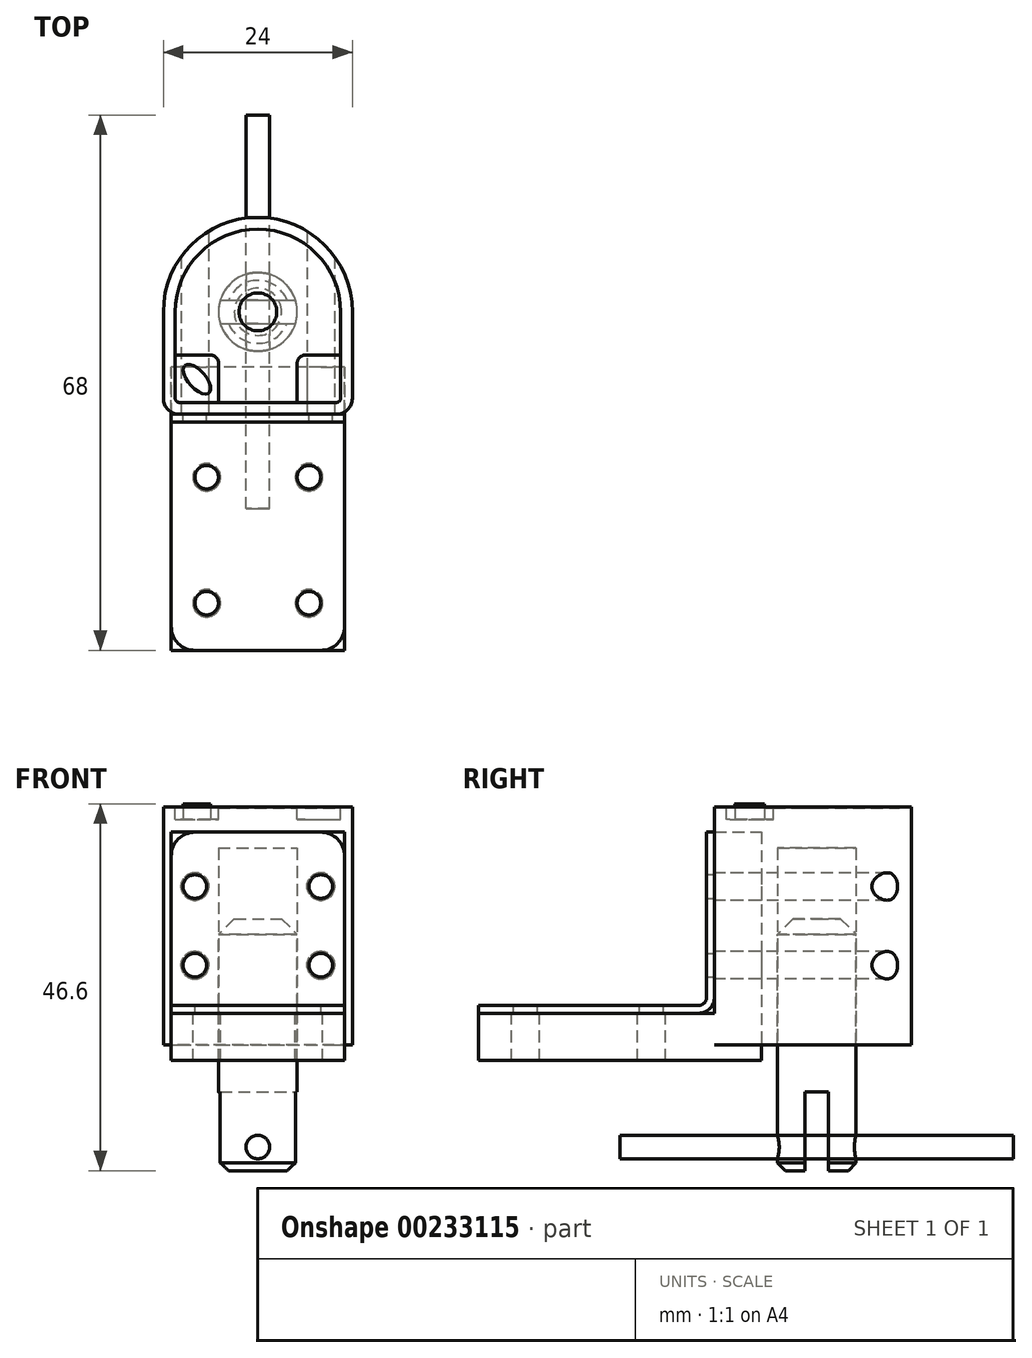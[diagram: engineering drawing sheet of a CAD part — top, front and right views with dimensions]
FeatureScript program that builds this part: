
annotation { "Feature Type Name" : "Feature", "Feature Type Description" : "" }
export const myFeature = defineFeature(function(context is Context, id is Id, definition is map)
    precondition{}
    {
        {
            var Q0;
            Q0=qCreatedBy(makeId("Top.planeOp"),FACE);
            var sketch = newSketch(context, id + "F0", { "sketchPlane" : qUnion([Q0])});
            skArc(sketch, "E0", {"start": v(12, 0) * mm, "mid": v(0, 12) * mm, "end": v(-12, 0) * mm});
            skLineSegment(sketch, "E1", {"start": v(-12, 0) * mm, "end": v(-12, -13) * mm});
            skLineSegment(sketch, "E2", {"start": v(-12, -13) * mm, "end": v(12, -13) * mm});
            skLineSegment(sketch, "E3", {"start": v(12, -13) * mm, "end": v(12, 0) * mm});
            skLineSegment(sketch, "E4", {"start": v(0, 12) * mm, "end": v(0, -13) * mm, "construction": true});
            skSolve(sketch);
        }
        {
            var Q0;
            Q0 = qSketchRegion(id + "F0", true);
            extrude(context, id + "F1", {"entities" : qUnion([Q0]), "oppositeDirection" : true, "depth" : 30.2 * mm});
        }
        {
            var Q0;
            Q0=makeQuery(id+"F1.opExtrude","CAP_FACE",FACE,{"disambiguationData":[OSD([sQuery(id+"F0.wireOp",EDGE,"E0"),sQuery(id+"F0.wireOp",EDGE,"E1"),sQuery(id+"F0.wireOp",EDGE,"E2"),sQuery(id+"F0.wireOp",EDGE,"E3")])],"isStart":false});
            var sketch = newSketch(context, id + "F2", { "sketchPlane" : qUnion([Q0])});
            skCircle(sketch, "E5", {"center": v(0, 0) * mm, "radius": 5 * mm});
            skSolve(sketch);
        }
        {
            var Q0;
            Q0 = qSketchRegion(id + "F2", true);
            extrude(context, id + "F3", {"entities" : qUnion([Q0]), "operationType" : NewBodyOperationType.REMOVE, "oppositeDirection" : true, "depth" : 25 * mm});
        }
        {
            var Q0;
            Q0 = qSketchRegion(id + "F2", true);
            extrude(context, id + "F4", {"entities" : qUnion([Q0]), "depth" : 32 * mm, "symmetric" : true});
        }
        {
            var Q0;
            Q0=makeQuery(id+"F1.opExtrude","SWEPT_EDGE",EDGE,{"disambiguationData":[OSD([sQuery(id+"F0.wireOp",EDGE,"E2"),sQuery(id+"F0.wireOp",EDGE,"E3")])]});
            var Q1;
            Q1=makeQuery(id+"F1.opExtrude","SWEPT_EDGE",EDGE,{"disambiguationData":[OSD([sQuery(id+"F0.wireOp",EDGE,"E1"),sQuery(id+"F0.wireOp",EDGE,"E2")])]});
            fillet(context, id + "F5", {"entities" : qUnion([Q0, Q1]), "radius" : 2 * mm, "tangentPropagation" : true, "allowEdgeOverflow" : false});
        }
        {
            var Q0;
            Q0=makeQuery(id+"F4.opExtrude","CAP_EDGE",EDGE,{"disambiguationData":[OSD([sQuery(id+"F2.wireOp",EDGE,"E5")])],"isStart":true});
            chamfer(context, id + "F6", {"entities" : qUnion([Q0]), "width" : 2 * mm, "tangentPropagation" : true});
        }
        {
            var Q0;
            Q0=makeQuery(id+"F4.opExtrude","CAP_EDGE",EDGE,{"disambiguationData":[OSD([sQuery(id+"F2.wireOp",EDGE,"E5")])],"isStart":false});
            chamfer(context, id + "F7", {"entities" : qUnion([Q0]), "width" : 1 * mm, "tangentPropagation" : true});
        }
        {
            var Q0;
            Q0=qCreatedBy(makeId("Right.planeOp"),FACE);
            var sketch = newSketch(context, id + "F8", { "sketchPlane" : qUnion([Q0])});
            skLineSegment(sketch, "E6.bottom", {"start": v(-1.5, -46.2) * mm, "end": v(1.5, -46.2) * mm});
            skLineSegment(sketch, "E6.top", {"start": v(-1.5, -36.2) * mm, "end": v(1.5, -36.2) * mm});
            skLineSegment(sketch, "E6.left", {"start": v(-1.5, -46.2) * mm, "end": v(-1.5, -36.2) * mm});
            skLineSegment(sketch, "E6.right", {"start": v(1.5, -46.2) * mm, "end": v(1.5, -36.2) * mm});
            skPoint(sketch, "E7", {"position": v(0, -46.2) * mm});
            skSolve(sketch);
        }
        {
            var Q0;
            Q0 = qSketchRegion(id + "F8", true);
            extrude(context, id + "F9", {"entities" : qUnion([Q0]), "operationType" : NewBodyOperationType.REMOVE, "oppositeDirection" : true, "depth" : 25 * mm, "symmetric" : true});
        }
        {
            var Q0;
            Q0=qCreatedBy(makeId("Front.planeOp"),FACE);
            var sketch = newSketch(context, id + "F10", { "sketchPlane" : qUnion([Q0])});
            skCircle(sketch, "E8", {"center": v(0, -43.2) * mm, "radius": 1.5 * mm});
            skSolve(sketch);
        }
        {
            var Q0;
            Q0 = qSketchRegion(id + "F10", true);
            extrude(context, id + "F11", {"entities" : qUnion([Q0]), "operationType" : NewBodyOperationType.REMOVE, "oppositeDirection" : true, "depth" : 25 * mm, "symmetric" : true});
        }
        {
            var Q0;
            Q0 = qSketchRegion(id + "F10", true);
            extrude(context, id + "F12", {"entities" : qUnion([Q0]), "depth" : 50 * mm, "symmetric" : true});
        }
        {
            var Q0;
            Q0=makeQuery(id+"F1.opExtrude","CAP_FACE",FACE,{"disambiguationData":[OSD([sQuery(id+"F0.wireOp",EDGE,"E0"),sQuery(id+"F0.wireOp",EDGE,"E1"),sQuery(id+"F0.wireOp",EDGE,"E2"),sQuery(id+"F0.wireOp",EDGE,"E3")])],"isStart":true});
            var sketch = newSketch(context, id + "F13", { "sketchPlane" : qUnion([Q0])});
            skArc(sketch, "E9.0", {"start": v(-10.5, -11) * mm, "mid": v(-10.35, -11.35) * mm, "end": v(-10, -11.5) * mm});
            skArc(sketch, "E9.1", {"start": v(10, -11.5) * mm, "mid": v(10.35, -11.35) * mm, "end": v(10.5, -11) * mm});
            skLineSegment(sketch, "E9.2", {"start": v(10.5, -11) * mm, "end": v(10.5, 0) * mm});
            skLineSegment(sketch, "E9.3", {"start": v(-10, -11.5) * mm, "end": v(10, -11.5) * mm});
            skArc(sketch, "E9.4", {"start": v(10.5, 0) * mm, "mid": v(0, 10.5) * mm, "end": v(-10.5, 0) * mm});
            skLineSegment(sketch, "E9.5", {"start": v(-10.5, 0) * mm, "end": v(-10.5, -11) * mm});
            skCircle(sketch, "E10", {"center": v(0, 0) * mm, "radius": 2.4 * mm});
            skSolve(sketch);
        }
        {
            var Q0;
            Q0 = qSketchRegion(id + "F13", true);
            extrude(context, id + "F14", {"entities" : qUnion([Q0]), "operationType" : NewBodyOperationType.REMOVE, "oppositeDirection" : true, "depth" : .1 * mm});
        }
        {
            var Q0;
            Q0=makeQuery(id+"F14.boolean.opBoolean","COPY",FACE,{"derivedFrom":makeQuery(id+"F14.opExtrude","CAP_FACE",FACE,{"disambiguationData":[OSD([sQuery(id+"F13.wireOp",EDGE,"E9.0"),sQuery(id+"F13.wireOp",EDGE,"E9.1"),sQuery(id+"F13.wireOp",EDGE,"E9.2"),sQuery(id+"F13.wireOp",EDGE,"E9.3"),sQuery(id+"F13.wireOp",EDGE,"E9.4"),sQuery(id+"F13.wireOp",EDGE,"E9.5"),sQuery(id+"F13.wireOp",EDGE,"E10")])],"isStart":false})});
            var sketch = newSketch(context, id + "F15", { "sketchPlane" : qUnion([Q0])});
            skLineSegment(sketch, "E11.left", {"start": v(-5, -6.5) * mm, "end": v(-5, -11.5) * mm});
            skLineSegment(sketch, "E11.right", {"start": v(5, -6.5) * mm, "end": v(5, -11.5) * mm});
            skLineSegment(sketch, "E12.trimOffspring", {"start": v(6, -5.5) * mm, "end": v(10.5, -5.5) * mm});
            skLineSegment(sketch, "E13", {"start": v(-6, -5.5) * mm, "end": v(-10.5, -5.5) * mm});
            skLineSegment(sketch, "E14.0", {"start": v(-10, -11.5) * mm, "end": v(-5, -11.5) * mm});
            skLineSegment(sketch, "E14.1", {"start": v(-10.5, -5.5) * mm, "end": v(-10.5, -11) * mm});
            skLineSegment(sketch, "E14.2", {"start": v(10.5, -11) * mm, "end": v(10.5, -5.5) * mm});
            skArc(sketch, "E14.3", {"start": v(10, -11.5) * mm, "mid": v(10.35, -11.35) * mm, "end": v(10.5, -11) * mm});
            skArc(sketch, "E14.4", {"start": v(-10.5, -11) * mm, "mid": v(-10.35, -11.35) * mm, "end": v(-10, -11.5) * mm});
            skPoint(sketch, "E15.orphan", {"position": v(-10.5, 0) * mm});
            skLineSegment(sketch, "E16.trimOffspring", {"start": v(5, -11.5) * mm, "end": v(10, -11.5) * mm});
            skPoint(sketch, "E17.orphan", {"position": v(10.5, 0) * mm});
            skPoint(sketch, "E18.visualSharp", {"position": v(-5, -5.5) * mm});
            skArc(sketch, "E18.filletArc", {"start": v(-5, -6.5) * mm, "mid": v(-5.3, -5.8) * mm, "end": v(-6, -5.5) * mm});
            skPoint(sketch, "E19.visualSharp", {"position": v(5, -5.5) * mm});
            skArc(sketch, "E19.filletArc", {"start": v(6, -5.5) * mm, "mid": v(5.3, -5.8) * mm, "end": v(5, -6.5) * mm});
            skLineSegment(sketch, "E20", {"start": v(-5, -11.5) * mm, "end": v(5, -11.5) * mm, "construction": true});
            skLineSegment(sketch, "E21", {"start": v(0, 0) * mm, "end": v(0, -11.5) * mm, "construction": true});
            skSolve(sketch);
        }
        {
            var Q0;
            Q0 = qSketchRegion(id + "F15", true);
            extrude(context, id + "F16", {"entities" : qUnion([Q0]), "operationType" : NewBodyOperationType.REMOVE, "oppositeDirection" : true, "depth" : 1.5 * mm});
        }
        {
            var Q0;
            Q0=makeQuery(id+"F16.boolean.opBoolean","COPY",FACE,{"derivedFrom":makeQuery(id+"F16.opExtrude","CAP_FACE",FACE,{"disambiguationData":[OSD([sQuery(id+"F15.wireOp",EDGE,"E11.left"),sQuery(id+"F15.wireOp",EDGE,"E13"),sQuery(id+"F15.wireOp",EDGE,"E14.0"),sQuery(id+"F15.wireOp",EDGE,"E14.1"),sQuery(id+"F15.wireOp",EDGE,"E14.4"),sQuery(id+"F15.wireOp",EDGE,"E18.filletArc")])],"isStart":false})});
            var sketch = newSketch(context, id + "F17", { "sketchPlane" : qUnion([Q0])});
            skEllipse(sketch, "E22", {"center": v(-7.75, -8.54) * mm, "majorRadius": 2.32 * mm, "minorRadius": 1.1 * mm, "majorAxis": v(-0.66, 0.75)});
            skLineSegment(sketch, "E23", {"start": v(-7.75, -8.54) * mm, "end": v(0, 0) * mm, "construction": true});
            skSolve(sketch);
        }
        {
            var Q0;
            Q0=makeQuery(id+"F1.opExtrude","SWEPT_FACE",FACE,{"disambiguationData":[OSD([sQuery(id+"F0.wireOp",EDGE,"E2")])]});
            var sketch = newSketch(context, id + "F18", { "sketchPlane" : qUnion([Q0])});
            skLineSegment(sketch, "E24", {"start": v(0, 0) * mm, "end": v(0, -30.2) * mm, "construction": true});
            skLineSegment(sketch, "E25.bottom", {"start": v(8, -10.1) * mm, "end": v(-8, -10.1) * mm, "construction": true});
            skLineSegment(sketch, "E25.top", {"start": v(8, -20.1) * mm, "end": v(-8, -20.1) * mm, "construction": true});
            skLineSegment(sketch, "E25.left", {"start": v(8, -10.1) * mm, "end": v(8, -20.1) * mm, "construction": true});
            skLineSegment(sketch, "E25.right", {"start": v(-8, -10.1) * mm, "end": v(-8, -20.1) * mm, "construction": true});
            skPoint(sketch, "E25.middle", {"position": v(0, -15.1) * mm});
            skCircle(sketch, "E26", {"center": v(-8, -10.1) * mm, "radius": 1.5 * mm});
            skCircle(sketch, "E27", {"center": v(8, -10.1) * mm, "radius": 1.5 * mm});
            skCircle(sketch, "E28", {"center": v(-8, -20.1) * mm, "radius": 1.5 * mm});
            skCircle(sketch, "E29", {"center": v(8, -20.1) * mm, "radius": 1.5 * mm});
            skSolve(sketch);
        }
        {
            var Q0;
            Q0 = qSketchRegion(id + "F18", true);
            extrude(context, id + "F19", {"entities" : qUnion([Q0]), "operationType" : NewBodyOperationType.REMOVE, "oppositeDirection" : true, "depth" : 3 * mm});
        }
        {
            var Q0;
            Q0 = qSketchRegion(id + "F17", true);
            extrude(context, id + "F20", {"entities" : qUnion([Q0]), "operationType" : NewBodyOperationType.ADD, "depth" : 2 * mm});
        }
        {
            var Q0;
            Q0=qCreatedBy(makeId("Right.planeOp"),FACE);
            var sketch = newSketch(context, id + "F21", { "sketchPlane" : qUnion([Q0])});
            skLineSegment(sketch, "E30", {"start": v(-13, -3.2) * mm, "end": v(-13, -24.2) * mm});
            skLineSegment(sketch, "E31", {"start": v(-15, -26.2) * mm, "end": v(-43, -26.2) * mm});
            skPoint(sketch, "E32.visualSharp", {"position": v(-13, -26.2) * mm});
            skArc(sketch, "E32.filletArc", {"start": v(-15, -26.2) * mm, "mid": v(-13.59, -25.61) * mm, "end": v(-13, -24.2) * mm});
            skLineSegment(sketch, "E33.0", {"start": v(-14, -3.2) * mm, "end": v(-14, -24.2) * mm});
            skArc(sketch, "E33.1", {"start": v(-15, -25.2) * mm, "mid": v(-14.3, -24.9) * mm, "end": v(-14, -24.2) * mm});
            skLineSegment(sketch, "E33.2", {"start": v(-15, -25.2) * mm, "end": v(-43, -25.2) * mm});
            skLineSegment(sketch, "E34", {"start": v(-14, -3.2) * mm, "end": v(-13, -3.2) * mm});
            skLineSegment(sketch, "E35", {"start": v(-43, -25.2) * mm, "end": v(-43, -26.2) * mm});
            skSolve(sketch);
        }
        {
            var Q0;
            Q0 = qSketchRegion(id + "F21", true);
            extrude(context, id + "F22", {"entities" : qUnion([Q0]), "depth" : 22 * mm, "symmetric" : true});
        }
        {
            var Q0;
            Q0 = qSketchRegion(id + "F18", true);
            extrude(context, id + "F23", {"entities" : qUnion([Q0]), "operationType" : NewBodyOperationType.REMOVE, "depth" : 3 * mm});
        }
        {
            var Q0;
            Q0=makeQuery(id+"F22.opExtrude","SWEPT_FACE",FACE,{"disambiguationData":[OSD([sQuery(id+"F21.wireOp",EDGE,"E33.2")])]});
            var sketch = newSketch(context, id + "F24", { "sketchPlane" : qUnion([Q0])});
            skLineSegment(sketch, "E36.bottom", {"start": v(6.5, -37) * mm, "end": v(-6.5, -37) * mm, "construction": true});
            skLineSegment(sketch, "E36.top", {"start": v(6.5, -21) * mm, "end": v(-6.5, -21) * mm, "construction": true});
            skLineSegment(sketch, "E36.left", {"start": v(6.5, -37) * mm, "end": v(6.5, -21) * mm, "construction": true});
            skLineSegment(sketch, "E36.right", {"start": v(-6.5, -37) * mm, "end": v(-6.5, -21) * mm, "construction": true});
            skPoint(sketch, "E36.middle", {"position": v(0, -29) * mm});
            skCircle(sketch, "E37", {"center": v(6.5, -21) * mm, "radius": 1.5 * mm});
            skCircle(sketch, "E38", {"center": v(6.5, -37) * mm, "radius": 1.5 * mm});
            skCircle(sketch, "E39", {"center": v(-6.5, -37) * mm, "radius": 1.5 * mm});
            skCircle(sketch, "E40", {"center": v(-6.5, -21) * mm, "radius": 1.5 * mm});
            skLineSegment(sketch, "E41", {"start": v(-11, -29) * mm, "end": v(11, -29) * mm, "construction": true});
            skSolve(sketch);
        }
        {
            var Q0;
            Q0 = qSketchRegion(id + "F24", true);
            var Q1;
            Q1=sQuery(id+"F24.wireOp",EDGE,"E37");
            extrude(context, id + "F25", {"entities" : qUnion([Q0]), "operationType" : NewBodyOperationType.REMOVE, "surfaceEntities" : qUnion([Q1]), "oppositeDirection" : true, "depth" : 25 * mm});
        }
        {
            var Q0;
            Q0=makeQuery(id+"F22.opExtrude","CAP_EDGE",EDGE,{"disambiguationData":[OSD([sQuery(id+"F21.wireOp",EDGE,"E34")])],"isStart":true});
            var Q1;
            Q1=makeQuery(id+"F22.opExtrude","CAP_EDGE",EDGE,{"disambiguationData":[OSD([sQuery(id+"F21.wireOp",EDGE,"E34")])],"isStart":false});
            var Q2;
            Q2=makeQuery(id+"F22.opExtrude","CAP_EDGE",EDGE,{"disambiguationData":[OSD([sQuery(id+"F21.wireOp",EDGE,"E35")])],"isStart":false});
            var Q3;
            Q3=makeQuery(id+"F22.opExtrude","CAP_EDGE",EDGE,{"disambiguationData":[OSD([sQuery(id+"F21.wireOp",EDGE,"E35")])],"isStart":true});
            fillet(context, id + "F26", {"entities" : qUnion([Q0, Q1, Q2, Q3]), "radius" : 3 * mm, "tangentPropagation" : true, "allowEdgeOverflow" : false});
        }
        {
            var Q0;
            Q0=qCreatedBy(makeId("Right.planeOp"),FACE);
            var sketch = newSketch(context, id + "F27", { "sketchPlane" : qUnion([Q0])});
            skLineSegment(sketch, "E42", {"start": v(-43, -26.2) * mm, "end": v(-13, -26.2) * mm});
            skLineSegment(sketch, "E43", {"start": v(-13, -26.2) * mm, "end": v(-13, -3.2) * mm});
            skLineSegment(sketch, "E44", {"start": v(-13, -3.2) * mm, "end": v(-7, -3.2) * mm});
            skLineSegment(sketch, "E45", {"start": v(-7, -3.2) * mm, "end": v(-7, -32.2) * mm});
            skLineSegment(sketch, "E46", {"start": v(-7, -32.2) * mm, "end": v(-43, -32.2) * mm});
            skLineSegment(sketch, "E47", {"start": v(-43, -32.2) * mm, "end": v(-43, -26.2) * mm});
            skSolve(sketch);
        }
        {
            var Q0;
            Q0 = qSketchRegion(id + "F27", true);
            extrude(context, id + "F28", {"entities" : qUnion([Q0]), "depth" : 22 * mm, "symmetric" : true});
        }
        {
            var Q0;
            Q0=makeQuery(id+"F28.opExtrude","SWEPT_FACE",FACE,{"disambiguationData":[OSD([sQuery(id+"F27.wireOp",EDGE,"E42")])]});
            var sketch = newSketch(context, id + "F29", { "sketchPlane" : qUnion([Q0])});
            skCircle(sketch, "E48", {"center": v(-6.5, -21) * mm, "radius": 1.75 * mm});
            skCircle(sketch, "E49", {"center": v(6.5, -21) * mm, "radius": 1.75 * mm});
            skCircle(sketch, "E50", {"center": v(-6.5, -37) * mm, "radius": 1.75 * mm});
            skCircle(sketch, "E51", {"center": v(6.5, -37) * mm, "radius": 1.75 * mm});
            skSolve(sketch);
        }
        {
            var Q0;
            Q0 = qSketchRegion(id + "F29", true);
            extrude(context, id + "F30", {"entities" : qUnion([Q0]), "operationType" : NewBodyOperationType.REMOVE, "oppositeDirection" : true, "depth" : 25 * mm});
        }
        {
            var Q0;
            Q0=makeQuery(id+"F28.opExtrude","SWEPT_FACE",FACE,{"disambiguationData":[OSD([sQuery(id+"F27.wireOp",EDGE,"E43")])]});
            var sketch = newSketch(context, id + "F31", { "sketchPlane" : qUnion([Q0])});
            skCircle(sketch, "E52", {"center": v(-8, -10.1) * mm, "radius": 1.75 * mm});
            skCircle(sketch, "E53", {"center": v(8, -10.1) * mm, "radius": 1.75 * mm});
            skCircle(sketch, "E54", {"center": v(8, -20.1) * mm, "radius": 1.75 * mm});
            skCircle(sketch, "E55", {"center": v(-8, -20.1) * mm, "radius": 1.75 * mm});
            skSolve(sketch);
        }
        {
            var Q0;
            Q0 = qSketchRegion(id + "F31", true);
            extrude(context, id + "F32", {"entities" : qUnion([Q0]), "operationType" : NewBodyOperationType.REMOVE, "oppositeDirection" : true, "depth" : 25 * mm});
        }
    });
